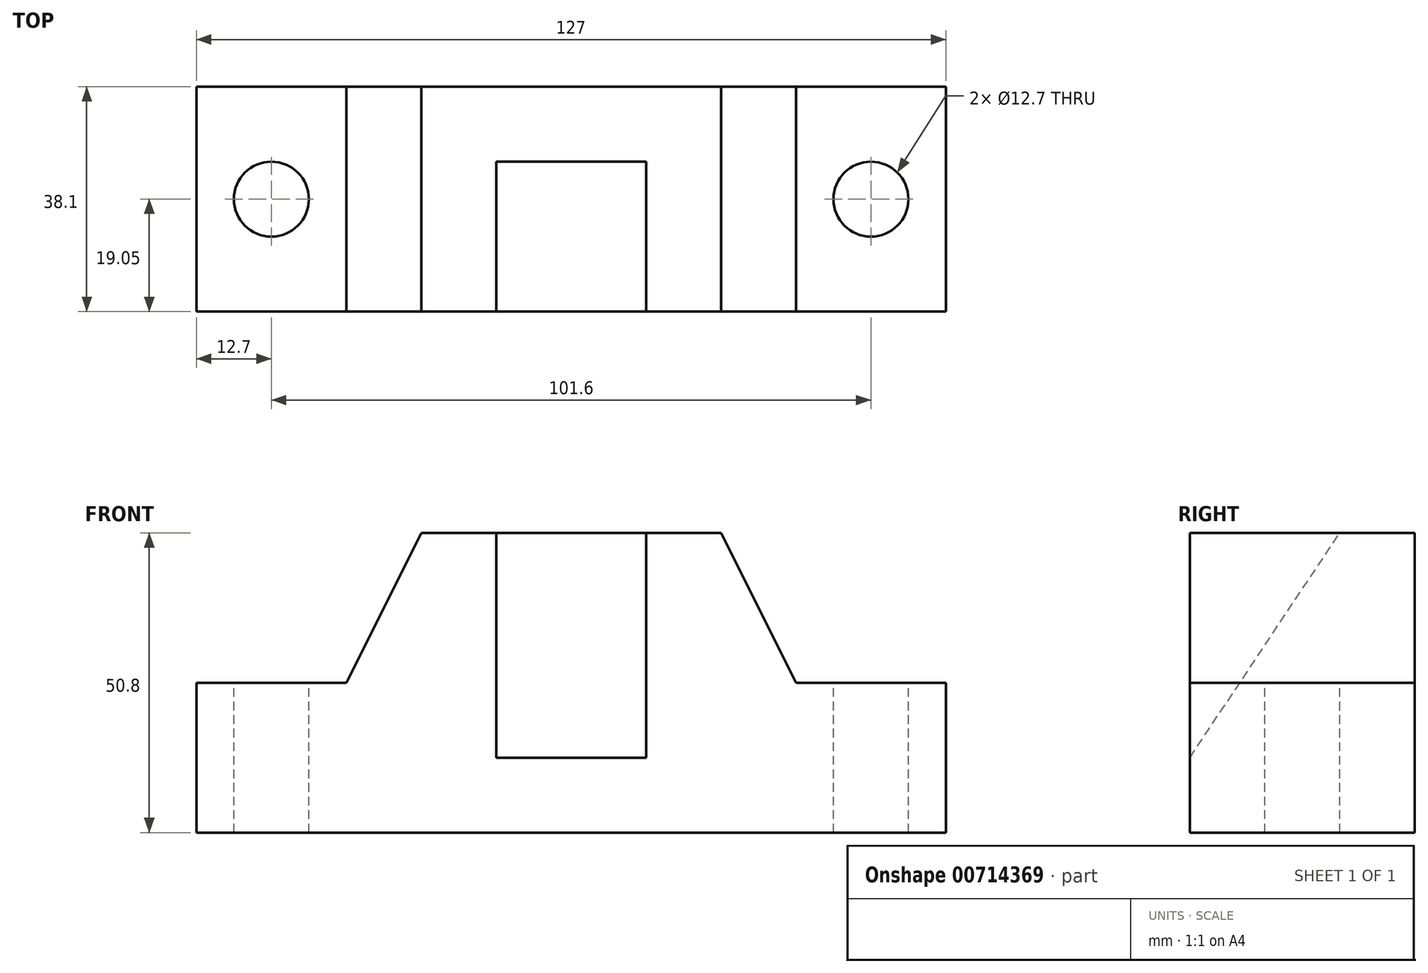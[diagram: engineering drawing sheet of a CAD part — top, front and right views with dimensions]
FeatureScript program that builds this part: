
annotation { "Feature Type Name" : "Feature", "Feature Type Description" : "" }
export const myFeature = defineFeature(function(context is Context, id is Id, definition is map)
    precondition{}
    {
        {
            var Q0;
            Q0=qCreatedBy(makeId("Front.planeOp"),FACE);
            var sketch = newSketch(context, id + "F0", { "sketchPlane" : qUnion([Q0])});
            skLineSegment(sketch, "E0.bottom", {"start": v(-49.47, 24.07) * mm, "end": v(77.53, 24.07) * mm});
            skLineSegment(sketch, "E0.top", {"start": v(-49.47, -26.73) * mm, "end": v(77.53, -26.73) * mm});
            skLineSegment(sketch, "E0.left", {"start": v(-49.47, 24.07) * mm, "end": v(-49.47, -26.73) * mm});
            skLineSegment(sketch, "E0.right", {"start": v(77.53, 24.07) * mm, "end": v(77.53, -26.73) * mm});
            skSolve(sketch);
        }
        {
            var Q0;
            Q0=qSketchRegion(id+"F0",true);
            extrude(context, id + "F1", {"entities" : qUnion([Q0]), "depth" : 38.1 * mm, "offsetDistance" : 25.4 * mm});
        }
        {
            var Q0;
            Q0=makeQuery(id+"F1.opExtrude","CAP_FACE",FACE,{"disambiguationData":[OSD([sQuery(id+"F0.wireOp",EDGE,"E0.bottom"),sQuery(id+"F0.wireOp",EDGE,"E0.top"),sQuery(id+"F0.wireOp",EDGE,"E0.left"),sQuery(id+"F0.wireOp",EDGE,"E0.right")])],"isStart":false});
            var sketch = newSketch(context, id + "F2", { "sketchPlane" : qUnion([Q0])});
            skLineSegment(sketch, "E1.bottom", {"start": v(-49.47, 24.07) * mm, "end": v(-24.07, 24.07) * mm});
            skLineSegment(sketch, "E1.top", {"start": v(-49.47, -1.33) * mm, "end": v(-24.07, -1.33) * mm});
            skLineSegment(sketch, "E1.left", {"start": v(-49.47, 24.07) * mm, "end": v(-49.47, -1.33) * mm});
            skLineSegment(sketch, "E1.right", {"start": v(-24.07, 24.07) * mm, "end": v(-24.07, -1.33) * mm});
            skLineSegment(sketch, "E2.bottom", {"start": v(77.53, 24.07) * mm, "end": v(52.13, 24.07) * mm});
            skLineSegment(sketch, "E2.top", {"start": v(77.53, -1.33) * mm, "end": v(52.13, -1.33) * mm});
            skLineSegment(sketch, "E2.left", {"start": v(77.53, 24.07) * mm, "end": v(77.53, -1.33) * mm});
            skLineSegment(sketch, "E2.right", {"start": v(52.13, 24.07) * mm, "end": v(52.13, -1.33) * mm});
            skSolve(sketch);
        }
        {
            var Q0;
            Q0=makeQuery(id+"F2.imprint","IMPRINT",FACE,{"disambiguationData":[TD([[makeQuery(id+"F2.imprint","IMPRINT",EDGE,{"derivedFrom":sQuery(id+"F2.wireOp",EDGE,"E1.bottom")}),-1.0]])]});
            var Q1;
            Q1=makeQuery(id+"F2.imprint","IMPRINT",FACE,{"disambiguationData":[TD([[makeQuery(id+"F2.imprint","IMPRINT",EDGE,{"derivedFrom":sQuery(id+"F2.wireOp",EDGE,"E2.bottom")}),-1.0]])]});
            extrude(context, id + "F3", {"entities" : qUnion([Q0, Q1]), "operationType" : NewBodyOperationType.REMOVE, "endBound" : BoundingType.THROUGH_ALL, "oppositeDirection" : true, "depth" : 25.4 * mm, "offsetDistance" : 25.4 * mm});
        }
        {
            var Q0;
            Q0=makeQuery(id+"F1.opExtrude","CAP_FACE",FACE,{"disambiguationData":[OSD([sQuery(id+"F0.wireOp",EDGE,"E0.bottom"),sQuery(id+"F0.wireOp",EDGE,"E0.top"),sQuery(id+"F0.wireOp",EDGE,"E0.left"),sQuery(id+"F0.wireOp",EDGE,"E0.right")])],"isStart":false});
            var sketch = newSketch(context, id + "F4", { "sketchPlane" : qUnion([Q0])});
            skLineSegment(sketch, "E3", {"start": v(-24.07, -1.33) * mm, "end": v(-11.37, 24.07) * mm});
            skLineSegment(sketch, "E4", {"start": v(-11.37, 24.07) * mm, "end": v(39.43, 24.07) * mm});
            skLineSegment(sketch, "E5", {"start": v(39.43, 24.07) * mm, "end": v(52.13, -1.33) * mm});
            skSolve(sketch);
        }
        {
            var Q0;
            {var subQ0=sQuery(id+"F4.wireOp",EDGE,"E3");Q0=makeQuery(id+"F4.imprint","IMPRINT",FACE,{"disambiguationData":[TD([[makeQuery(id+"F4.imprint","IMPRINT",EDGE,{"derivedFrom":subQ0}),1.0]])]});}
            var Q1;
            {var subQ0=sQuery(id+"F4.wireOp",EDGE,"E5");Q1=makeQuery(id+"F4.imprint","IMPRINT",FACE,{"disambiguationData":[TD([[makeQuery(id+"F4.imprint","IMPRINT",EDGE,{"derivedFrom":subQ0}),1.0]])]});}
            extrude(context, id + "F5", {"entities" : qUnion([Q0, Q1]), "operationType" : NewBodyOperationType.REMOVE, "endBound" : BoundingType.THROUGH_ALL, "oppositeDirection" : true, "depth" : 25.4 * mm, "offsetDistance" : 25.4 * mm});
        }
        {
            var Q0;
            Q0=makeQuery(id+"F1.opExtrude","CAP_FACE",FACE,{"disambiguationData":[OSD([sQuery(id+"F0.wireOp",EDGE,"E0.bottom"),sQuery(id+"F0.wireOp",EDGE,"E0.top"),sQuery(id+"F0.wireOp",EDGE,"E0.left"),sQuery(id+"F0.wireOp",EDGE,"E0.right")])],"isStart":false});
            var sketch = newSketch(context, id + "F6", { "sketchPlane" : qUnion([Q0])});
            skLineSegment(sketch, "E6.bottom", {"start": v(1.33, 24.07) * mm, "end": v(26.73, 24.07) * mm});
            skLineSegment(sketch, "E6.top", {"start": v(1.33, -14.03) * mm, "end": v(26.73, -14.03) * mm});
            skLineSegment(sketch, "E6.left", {"start": v(1.33, 24.07) * mm, "end": v(1.33, -14.03) * mm});
            skLineSegment(sketch, "E6.right", {"start": v(26.73, 24.07) * mm, "end": v(26.73, -14.03) * mm});
            skSolve(sketch);
        }
        {
            var Q0;
            Q0=makeQuery(id+"F3.boolean.opBoolean","COPY",FACE,{"derivedFrom":makeQuery(id+"F3.opExtrude","SWEPT_FACE",FACE,{"disambiguationData":[OSD([sQuery(id+"F2.wireOp",EDGE,"E1.top")])]})});
            var sketch = newSketch(context, id + "F7", { "sketchPlane" : qUnion([Q0])});
            skCircle(sketch, "E7", {"center": v(-36.77, -19.05) * mm, "radius": 6.35 * mm});
            skSolve(sketch);
        }
        {
            var Q0;
            Q0=makeQuery(id+"F3.boolean.opBoolean","COPY",FACE,{"derivedFrom":makeQuery(id+"F3.opExtrude","SWEPT_FACE",FACE,{"disambiguationData":[OSD([sQuery(id+"F2.wireOp",EDGE,"E2.top")])]})});
            var sketch = newSketch(context, id + "F8", { "sketchPlane" : qUnion([Q0])});
            skCircle(sketch, "E8", {"center": v(64.83, -19.05) * mm, "radius": 6.35 * mm});
            skSolve(sketch);
        }
        {
            var Q0;
            Q0=makeQuery(id+"F8.imprint","IMPRINT",FACE,{"disambiguationData":[TD([[makeQuery(id+"F8.imprint","IMPRINT",EDGE,{"derivedFrom":sQuery(id+"F8.wireOp",EDGE,"E8")}),1.0]])]});
            var Q1;
            Q1=makeQuery(id+"F7.imprint","IMPRINT",FACE,{"disambiguationData":[TD([[makeQuery(id+"F7.imprint","IMPRINT",EDGE,{"derivedFrom":sQuery(id+"F7.wireOp",EDGE,"E7")}),1.0]])]});
            extrude(context, id + "F9", {"entities" : qUnion([Q0, Q1]), "operationType" : NewBodyOperationType.REMOVE, "endBound" : BoundingType.THROUGH_ALL, "oppositeDirection" : true, "depth" : 25.4 * mm, "offsetDistance" : 25.4 * mm});
        }
        {
            var Q0;
            Q0=makeQuery(id+"F6.imprint","IMPRINT",FACE,{"disambiguationData":[TD([[makeQuery(id+"F6.imprint","IMPRINT",EDGE,{"derivedFrom":sQuery(id+"F6.wireOp",EDGE,"E6.bottom")}),-1.0]])]});
            extrude(context, id + "F10", {"entities" : qUnion([Q0]), "operationType" : NewBodyOperationType.REMOVE, "oppositeDirection" : true, "depth" : 25.4 * mm, "offsetDistance" : 25.4 * mm});
        }
        {
            var Q0;
            Q0=makeQuery(id+"F10.boolean.opBoolean","COPY",FACE,{"derivedFrom":makeQuery(id+"F10.opExtrude","SWEPT_FACE",FACE,{"disambiguationData":[OSD([sQuery(id+"F6.wireOp",EDGE,"E6.left")])]})});
            var sketch = newSketch(context, id + "F11", { "sketchPlane" : qUnion([Q0])});
            skLineSegment(sketch, "E9", {"start": v(-38.1, -14.03) * mm, "end": v(-12.7, 24.07) * mm});
            skSolve(sketch);
        }
        {
            var Q0;
            Q0=makeQuery(id+"F11.imprint","IMPRINT",FACE,{"disambiguationData":[TD([[makeQuery(id+"F11.imprint","IMPRINT",EDGE,{"derivedFrom":sQuery(id+"F11.wireOp",EDGE,"E9")}),-1.0]])]});
            extrude(context, id + "F12", {"entities" : qUnion([Q0]), "operationType" : NewBodyOperationType.ADD, "depth" : 25.4 * mm, "offsetDistance" : 25.4 * mm});
        }
    });
